# Revit family: AFX-Remy-Outdoor_Sconce-1
name_source: partatom
category: Lighting Fixtures
units: mm (PartAtom-declared; Revit-internal decimal feet)

## family parameters
Cut with Voids When Loaded = No
Host = Face
Light Source = Yes
Part Type = Normal
Room Calculation Point = No
Round Connector Dimension = Use Diameter
Shared = No

## types (2) — shared parameters
Apparent Load = 0 VA
Assembly Code = D5020200
Color Filter = 16777215
Colour Rendering Index = 80
Default Elevation = 48"
Depth = 2 1/8"
Diffuser Finish = AFX - White Acrylic
Dimming Lamp Color Temperature Shift = <None>
Emit Shape Visible in Rendering = No
Frame Finish = AFX - Black Steel
Keynote = 12500
Lamp = LED
Manufacturer = AFX Inc
Power Factor = 1
Product Documentation Link = https://www.afxinc.com
Tilt Angle = 0.00°
Type Comments = Remy
URL = https://www.afxinc.com
Voltage = 120 V
Wattage Comments = 9

## per-type parameters (varying)
| type | 10inch | 7inch | Description | Emit from Circle Diameter | Height | Photometric Web File | Width |
| REMW0407LAJMVBK | No | Yes | LED Outdoor Sconce - 4 3/4"W x 2 1/8"D x 7 1/2"H | 4" | 7 1/2" | REMW0407LAJMVBK_3000K_IES.IES | 4 3/4" |
| REMW0610LAJMVBK | Yes | No | LED Outdoor Sconce - 5 1/2"W x 2 1/8"D x 10"H | 5" | 10" | REMW0610LAJMVBK_3000K_IES.IES | 5 1/2" |

note: column(s) folded — value = type name in every type: Model

## geometry (parser evidence)
native form markers: Sweep x2
no freeform markers — native parametric forms only
